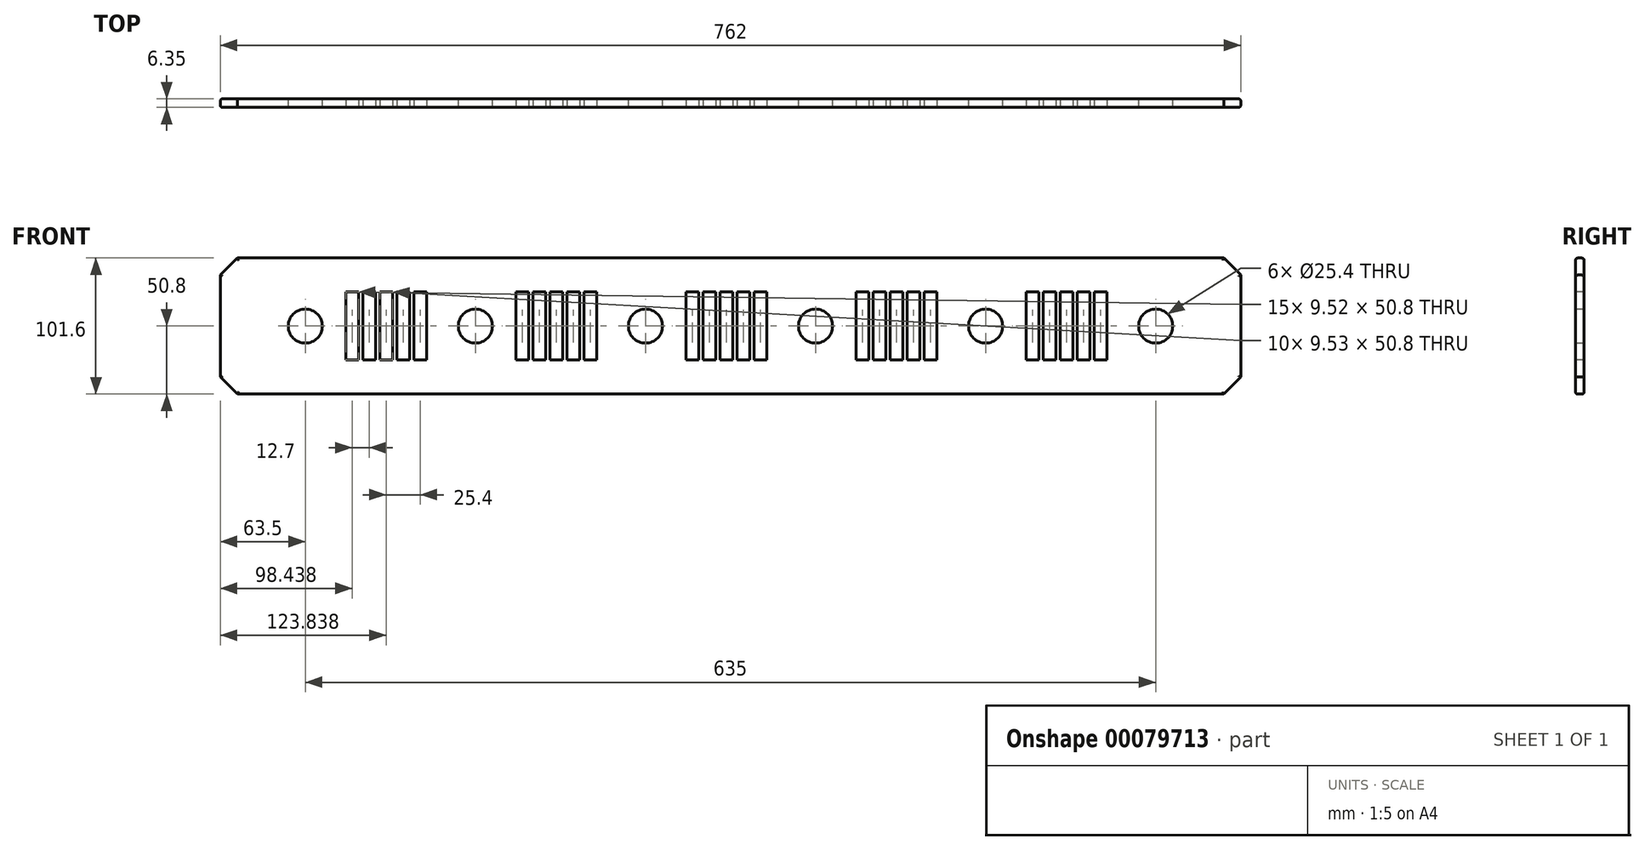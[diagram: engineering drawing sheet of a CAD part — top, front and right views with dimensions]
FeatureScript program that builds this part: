
annotation { "Feature Type Name" : "Feature", "Feature Type Description" : "" }
export const myFeature = defineFeature(function(context is Context, id is Id, definition is map)
    precondition{}
    {
        {
            var Q0;
            Q0=qCreatedBy(makeId("Front.planeOp"),FACE);
            var sketch = newSketch(context, id + "F0", { "sketchPlane" : qUnion([Q0])});
            skLineSegment(sketch, "E0.bottom", {"start": v(0, 0) * mm, "end": v(762, 0) * mm});
            skLineSegment(sketch, "E0.top", {"start": v(0, 101.6) * mm, "end": v(762, 101.6) * mm});
            skLineSegment(sketch, "E0.left", {"start": v(0, 0) * mm, "end": v(0, 101.6) * mm});
            skLineSegment(sketch, "E0.right", {"start": v(762, 0) * mm, "end": v(762, 101.6) * mm});
            skCircle(sketch, "E1", {"center": v(63.5, 50.8) * mm, "radius": 12.7 * mm});
            skPoint(sketch, "E1.centerSnap0", {"position": v(0, 50.8) * mm});
            skCircle(sketch, "E2", {"center": v(190.5, 50.8) * mm, "radius": 12.7 * mm});
            skCircle(sketch, "E3", {"center": v(317.5, 50.8) * mm, "radius": 12.7 * mm});
            skCircle(sketch, "E4", {"center": v(444.5, 50.8) * mm, "radius": 12.7 * mm});
            skCircle(sketch, "E5", {"center": v(571.5, 50.8) * mm, "radius": 12.7 * mm});
            skCircle(sketch, "E6", {"center": v(698.5, 50.8) * mm, "radius": 12.7 * mm});
            skSolve(sketch);
        }
        {
            var Q0;
            Q0 = qSketchRegion(id + "F0", true);
            extrude(context, id + "F1", {"entities" : qUnion([Q0]), "depth" : 6.35 * mm});
        }
        {
            var Q0;
            Q0=makeQuery(id+"F1.opExtrude","CAP_FACE",FACE,{"disambiguationData":[OSD([sQuery(id+"F0.wireOp",EDGE,"E0.bottom"),sQuery(id+"F0.wireOp",EDGE,"E0.top"),sQuery(id+"F0.wireOp",EDGE,"E0.left"),sQuery(id+"F0.wireOp",EDGE,"E0.right"),sQuery(id+"F0.wireOp",EDGE,"E1"),sQuery(id+"F0.wireOp",EDGE,"E2"),sQuery(id+"F0.wireOp",EDGE,"E3"),sQuery(id+"F0.wireOp",EDGE,"E4"),sQuery(id+"F0.wireOp",EDGE,"E5"),sQuery(id+"F0.wireOp",EDGE,"E6")])],"isStart":false});
            var sketch = newSketch(context, id + "F2", { "sketchPlane" : qUnion([Q0])});
            skLineSegment(sketch, "E7.bottom", {"start": v(93.68, 76.2) * mm, "end": v(103.2, 76.2) * mm});
            skLineSegment(sketch, "E7.top", {"start": v(93.68, 25.4) * mm, "end": v(103.2, 25.4) * mm});
            skLineSegment(sketch, "E7.left", {"start": v(93.68, 76.2) * mm, "end": v(93.68, 25.4) * mm});
            skLineSegment(sketch, "E7.right", {"start": v(103.2, 76.2) * mm, "end": v(103.2, 25.4) * mm});
            skLineSegment(sketch, "E8.1.0.0", {"start": v(106.38, 76.2) * mm, "end": v(115.9, 76.2) * mm});
            skLineSegment(sketch, "E8.1.0.1", {"start": v(106.38, 25.4) * mm, "end": v(115.9, 25.4) * mm});
            skLineSegment(sketch, "E8.1.0.2", {"start": v(106.38, 76.2) * mm, "end": v(106.38, 25.4) * mm});
            skLineSegment(sketch, "E8.1.0.3", {"start": v(115.9, 76.2) * mm, "end": v(115.9, 25.4) * mm});
            skLineSegment(sketch, "E8.2.0.0", {"start": v(119.08, 76.2) * mm, "end": v(128.6, 76.2) * mm});
            skLineSegment(sketch, "E8.2.0.1", {"start": v(119.08, 25.4) * mm, "end": v(128.6, 25.4) * mm});
            skLineSegment(sketch, "E8.2.0.2", {"start": v(119.08, 76.2) * mm, "end": v(119.08, 25.4) * mm});
            skLineSegment(sketch, "E8.2.0.3", {"start": v(128.6, 76.2) * mm, "end": v(128.6, 25.4) * mm});
            skLineSegment(sketch, "E8.3.0.0", {"start": v(131.78, 76.2) * mm, "end": v(141.3, 76.2) * mm});
            skLineSegment(sketch, "E8.3.0.1", {"start": v(131.78, 25.4) * mm, "end": v(141.3, 25.4) * mm});
            skLineSegment(sketch, "E8.3.0.2", {"start": v(131.78, 76.2) * mm, "end": v(131.78, 25.4) * mm});
            skLineSegment(sketch, "E8.3.0.3", {"start": v(141.3, 76.2) * mm, "end": v(141.3, 25.4) * mm});
            skLineSegment(sketch, "E8.4.0.0", {"start": v(144.48, 76.2) * mm, "end": v(154, 76.2) * mm});
            skLineSegment(sketch, "E8.4.0.1", {"start": v(144.48, 25.4) * mm, "end": v(154, 25.4) * mm});
            skLineSegment(sketch, "E8.4.0.2", {"start": v(144.48, 76.2) * mm, "end": v(144.48, 25.4) * mm});
            skLineSegment(sketch, "E8.4.0.3", {"start": v(154, 76.2) * mm, "end": v(154, 25.4) * mm});
            skLineSegment(sketch, "E8.direction1", {"start": v(93.68, 76.2) * mm, "end": v(106.38, 76.2) * mm, "construction": true});
            skLineSegment(sketch, "E9.bottom", {"start": v(220.68, 76.2) * mm, "end": v(230.2, 76.2) * mm});
            skLineSegment(sketch, "E9.top", {"start": v(220.68, 25.4) * mm, "end": v(230.2, 25.4) * mm});
            skLineSegment(sketch, "E9.left", {"start": v(220.68, 76.2) * mm, "end": v(220.68, 25.4) * mm});
            skLineSegment(sketch, "E9.right", {"start": v(230.2, 76.2) * mm, "end": v(230.2, 25.4) * mm});
            skLineSegment(sketch, "E10.1.0.0", {"start": v(233.38, 76.2) * mm, "end": v(233.38, 25.4) * mm});
            skLineSegment(sketch, "E10.1.0.1", {"start": v(242.9, 76.2) * mm, "end": v(242.9, 25.4) * mm});
            skLineSegment(sketch, "E10.1.0.2", {"start": v(233.38, 76.2) * mm, "end": v(242.9, 76.2) * mm});
            skLineSegment(sketch, "E10.1.0.3", {"start": v(233.38, 25.4) * mm, "end": v(242.9, 25.4) * mm});
            skLineSegment(sketch, "E10.2.0.0", {"start": v(246.08, 76.2) * mm, "end": v(246.08, 25.4) * mm});
            skLineSegment(sketch, "E10.2.0.1", {"start": v(255.6, 76.2) * mm, "end": v(255.6, 25.4) * mm});
            skLineSegment(sketch, "E10.2.0.2", {"start": v(246.08, 76.2) * mm, "end": v(255.6, 76.2) * mm});
            skLineSegment(sketch, "E10.2.0.3", {"start": v(246.08, 25.4) * mm, "end": v(255.6, 25.4) * mm});
            skLineSegment(sketch, "E10.3.0.0", {"start": v(258.78, 76.2) * mm, "end": v(258.78, 25.4) * mm});
            skLineSegment(sketch, "E10.3.0.1", {"start": v(268.3, 76.2) * mm, "end": v(268.3, 25.4) * mm});
            skLineSegment(sketch, "E10.3.0.2", {"start": v(258.78, 76.2) * mm, "end": v(268.3, 76.2) * mm});
            skLineSegment(sketch, "E10.3.0.3", {"start": v(258.78, 25.4) * mm, "end": v(268.3, 25.4) * mm});
            skLineSegment(sketch, "E10.4.0.0", {"start": v(271.48, 76.2) * mm, "end": v(271.48, 25.4) * mm});
            skLineSegment(sketch, "E10.4.0.1", {"start": v(281, 76.2) * mm, "end": v(281, 25.4) * mm});
            skLineSegment(sketch, "E10.4.0.2", {"start": v(271.48, 76.2) * mm, "end": v(281, 76.2) * mm});
            skLineSegment(sketch, "E10.4.0.3", {"start": v(271.48, 25.4) * mm, "end": v(281, 25.4) * mm});
            skLineSegment(sketch, "E10.direction1", {"start": v(220.68, 25.4) * mm, "end": v(233.38, 25.4) * mm, "construction": true});
            skLineSegment(sketch, "E11.bottom", {"start": v(347.68, 76.2) * mm, "end": v(357.2, 76.2) * mm});
            skLineSegment(sketch, "E11.top", {"start": v(347.68, 25.4) * mm, "end": v(357.2, 25.4) * mm});
            skLineSegment(sketch, "E11.left", {"start": v(347.68, 76.2) * mm, "end": v(347.68, 25.4) * mm});
            skLineSegment(sketch, "E11.right", {"start": v(357.2, 76.2) * mm, "end": v(357.2, 25.4) * mm});
            skLineSegment(sketch, "E12.1.0.0", {"start": v(360.38, 76.2) * mm, "end": v(369.9, 76.2) * mm});
            skLineSegment(sketch, "E12.1.0.1", {"start": v(360.38, 25.4) * mm, "end": v(369.9, 25.4) * mm});
            skLineSegment(sketch, "E12.1.0.2", {"start": v(360.38, 76.2) * mm, "end": v(360.38, 25.4) * mm});
            skLineSegment(sketch, "E12.1.0.3", {"start": v(369.9, 76.2) * mm, "end": v(369.9, 25.4) * mm});
            skLineSegment(sketch, "E12.2.0.0", {"start": v(373.08, 76.2) * mm, "end": v(382.6, 76.2) * mm});
            skLineSegment(sketch, "E12.2.0.1", {"start": v(373.08, 25.4) * mm, "end": v(382.6, 25.4) * mm});
            skLineSegment(sketch, "E12.2.0.2", {"start": v(373.08, 76.2) * mm, "end": v(373.08, 25.4) * mm});
            skLineSegment(sketch, "E12.2.0.3", {"start": v(382.6, 76.2) * mm, "end": v(382.6, 25.4) * mm});
            skLineSegment(sketch, "E12.3.0.0", {"start": v(385.78, 76.2) * mm, "end": v(395.3, 76.2) * mm});
            skLineSegment(sketch, "E12.3.0.1", {"start": v(385.78, 25.4) * mm, "end": v(395.3, 25.4) * mm});
            skLineSegment(sketch, "E12.3.0.2", {"start": v(385.78, 76.2) * mm, "end": v(385.78, 25.4) * mm});
            skLineSegment(sketch, "E12.3.0.3", {"start": v(395.3, 76.2) * mm, "end": v(395.3, 25.4) * mm});
            skLineSegment(sketch, "E12.4.0.0", {"start": v(398.48, 76.2) * mm, "end": v(408, 76.2) * mm});
            skLineSegment(sketch, "E12.4.0.1", {"start": v(398.48, 25.4) * mm, "end": v(408, 25.4) * mm});
            skLineSegment(sketch, "E12.4.0.2", {"start": v(398.48, 76.2) * mm, "end": v(398.48, 25.4) * mm});
            skLineSegment(sketch, "E12.4.0.3", {"start": v(408, 76.2) * mm, "end": v(408, 25.4) * mm});
            skLineSegment(sketch, "E12.direction1", {"start": v(347.68, 76.2) * mm, "end": v(360.38, 76.2) * mm, "construction": true});
            skLineSegment(sketch, "E13.bottom", {"start": v(474.68, 76.2) * mm, "end": v(484.2, 76.2) * mm});
            skLineSegment(sketch, "E13.top", {"start": v(474.68, 25.4) * mm, "end": v(484.2, 25.4) * mm});
            skLineSegment(sketch, "E13.left", {"start": v(474.68, 76.2) * mm, "end": v(474.68, 25.4) * mm});
            skLineSegment(sketch, "E13.right", {"start": v(484.2, 76.2) * mm, "end": v(484.2, 25.4) * mm});
            skLineSegment(sketch, "E14.1.0.0", {"start": v(487.38, 76.2) * mm, "end": v(487.38, 25.4) * mm});
            skLineSegment(sketch, "E14.1.0.1", {"start": v(496.9, 76.2) * mm, "end": v(496.9, 25.4) * mm});
            skLineSegment(sketch, "E14.1.0.2", {"start": v(487.38, 76.2) * mm, "end": v(496.9, 76.2) * mm});
            skLineSegment(sketch, "E14.1.0.3", {"start": v(487.38, 25.4) * mm, "end": v(496.9, 25.4) * mm});
            skLineSegment(sketch, "E14.2.0.0", {"start": v(500.08, 76.2) * mm, "end": v(500.08, 25.4) * mm});
            skLineSegment(sketch, "E14.2.0.1", {"start": v(509.6, 76.2) * mm, "end": v(509.6, 25.4) * mm});
            skLineSegment(sketch, "E14.2.0.2", {"start": v(500.08, 76.2) * mm, "end": v(509.6, 76.2) * mm});
            skLineSegment(sketch, "E14.2.0.3", {"start": v(500.08, 25.4) * mm, "end": v(509.6, 25.4) * mm});
            skLineSegment(sketch, "E14.3.0.0", {"start": v(512.78, 76.2) * mm, "end": v(512.78, 25.4) * mm});
            skLineSegment(sketch, "E14.3.0.1", {"start": v(522.3, 76.2) * mm, "end": v(522.3, 25.4) * mm});
            skLineSegment(sketch, "E14.3.0.2", {"start": v(512.78, 76.2) * mm, "end": v(522.3, 76.2) * mm});
            skLineSegment(sketch, "E14.3.0.3", {"start": v(512.78, 25.4) * mm, "end": v(522.3, 25.4) * mm});
            skLineSegment(sketch, "E14.4.0.0", {"start": v(525.48, 76.2) * mm, "end": v(525.48, 25.4) * mm});
            skLineSegment(sketch, "E14.4.0.1", {"start": v(535, 76.2) * mm, "end": v(535, 25.4) * mm});
            skLineSegment(sketch, "E14.4.0.2", {"start": v(525.48, 76.2) * mm, "end": v(535, 76.2) * mm});
            skLineSegment(sketch, "E14.4.0.3", {"start": v(525.48, 25.4) * mm, "end": v(535, 25.4) * mm});
            skLineSegment(sketch, "E14.direction1", {"start": v(474.68, 25.4) * mm, "end": v(487.38, 25.4) * mm, "construction": true});
            skLineSegment(sketch, "E15.bottom", {"start": v(601.68, 76.2) * mm, "end": v(611.2, 76.2) * mm});
            skLineSegment(sketch, "E15.top", {"start": v(601.68, 25.4) * mm, "end": v(611.2, 25.4) * mm});
            skLineSegment(sketch, "E15.left", {"start": v(601.68, 76.2) * mm, "end": v(601.68, 25.4) * mm});
            skLineSegment(sketch, "E15.right", {"start": v(611.2, 76.2) * mm, "end": v(611.2, 25.4) * mm});
            skLineSegment(sketch, "E16.1.0.0", {"start": v(614.38, 76.2) * mm, "end": v(623.9, 76.2) * mm});
            skLineSegment(sketch, "E16.1.0.1", {"start": v(614.38, 76.2) * mm, "end": v(614.38, 25.4) * mm});
            skLineSegment(sketch, "E16.1.0.2", {"start": v(623.9, 76.2) * mm, "end": v(623.9, 25.4) * mm});
            skLineSegment(sketch, "E16.1.0.3", {"start": v(614.38, 25.4) * mm, "end": v(623.9, 25.4) * mm});
            skLineSegment(sketch, "E16.2.0.0", {"start": v(627.08, 76.2) * mm, "end": v(636.6, 76.2) * mm});
            skLineSegment(sketch, "E16.2.0.1", {"start": v(627.08, 76.2) * mm, "end": v(627.08, 25.4) * mm});
            skLineSegment(sketch, "E16.2.0.2", {"start": v(636.6, 76.2) * mm, "end": v(636.6, 25.4) * mm});
            skLineSegment(sketch, "E16.2.0.3", {"start": v(627.08, 25.4) * mm, "end": v(636.6, 25.4) * mm});
            skLineSegment(sketch, "E16.3.0.0", {"start": v(639.78, 76.2) * mm, "end": v(649.3, 76.2) * mm});
            skLineSegment(sketch, "E16.3.0.1", {"start": v(639.78, 76.2) * mm, "end": v(639.78, 25.4) * mm});
            skLineSegment(sketch, "E16.3.0.2", {"start": v(649.3, 76.2) * mm, "end": v(649.3, 25.4) * mm});
            skLineSegment(sketch, "E16.3.0.3", {"start": v(639.78, 25.4) * mm, "end": v(649.3, 25.4) * mm});
            skLineSegment(sketch, "E16.4.0.0", {"start": v(652.48, 76.2) * mm, "end": v(662, 76.2) * mm});
            skLineSegment(sketch, "E16.4.0.1", {"start": v(652.48, 76.2) * mm, "end": v(652.48, 25.4) * mm});
            skLineSegment(sketch, "E16.4.0.2", {"start": v(662, 76.2) * mm, "end": v(662, 25.4) * mm});
            skLineSegment(sketch, "E16.4.0.3", {"start": v(652.48, 25.4) * mm, "end": v(662, 25.4) * mm});
            skLineSegment(sketch, "E16.direction1", {"start": v(601.68, 76.2) * mm, "end": v(614.38, 76.2) * mm, "construction": true});
            skSolve(sketch);
        }
        {
            var Q0;
            Q0 = qSketchRegion(id + "F2", true);
            extrude(context, id + "F3", {"entities" : qUnion([Q0]), "operationType" : NewBodyOperationType.REMOVE, "endBound" : BoundingType.THROUGH_ALL, "oppositeDirection" : true, "depth" : 25.4 * mm});
        }
        {
            var Q0;
            Q0=makeQuery(id+"F1.opExtrude","SWEPT_EDGE",EDGE,{"disambiguationData":[OSD([sQuery(id+"F0.wireOp",EDGE,"E0.top"),sQuery(id+"F0.wireOp",EDGE,"E0.left")])]});
            var Q1;
            Q1=makeQuery(id+"F1.opExtrude","SWEPT_EDGE",EDGE,{"disambiguationData":[OSD([sQuery(id+"F0.wireOp",EDGE,"E0.bottom"),sQuery(id+"F0.wireOp",EDGE,"E0.left")])]});
            var Q2;
            Q2=makeQuery(id+"F1.opExtrude","SWEPT_EDGE",EDGE,{"disambiguationData":[OSD([sQuery(id+"F0.wireOp",EDGE,"E0.top"),sQuery(id+"F0.wireOp",EDGE,"E0.right")])]});
            var Q3;
            Q3=makeQuery(id+"F1.opExtrude","SWEPT_EDGE",EDGE,{"disambiguationData":[OSD([sQuery(id+"F0.wireOp",EDGE,"E0.bottom"),sQuery(id+"F0.wireOp",EDGE,"E0.right")])]});
            chamfer(context, id + "F4", {"entities" : qUnion([Q0, Q1, Q2, Q3]), "width" : 12.7 * mm, "tangentPropagation" : true});
        }
        {
            var Q0;
            Q0=makeQuery(id+"F1.opExtrude","CAP_EDGE",EDGE,{"disambiguationData":[OSD([sQuery(id+"F0.wireOp",EDGE,"E0.top")])],"isStart":false});
            var Q1;
            Q1=makeQuery(id+"F1.opExtrude","CAP_EDGE",EDGE,{"disambiguationData":[OSD([sQuery(id+"F0.wireOp",EDGE,"E0.top")])],"isStart":true});
            var Q2;
            Q2=makeQuery(id+"F1.opExtrude","CAP_EDGE",EDGE,{"disambiguationData":[OSD([sQuery(id+"F0.wireOp",EDGE,"E0.bottom")])],"isStart":false});
            var Q3;
            Q3=makeQuery(id+"F1.opExtrude","CAP_EDGE",EDGE,{"disambiguationData":[OSD([sQuery(id+"F0.wireOp",EDGE,"E0.bottom")])],"isStart":true});
            var Q4;
            {var subQ0=sQuery(id+"F0.wireOp",EDGE,"E0.left");var subQ1=sQuery(id+"F0.wireOp",EDGE,"E0.top");Q4=makeQuery(id+"F4.opChamfer","BLEND_EDGE",EDGE,{"blendedFrom":[makeQuery(id+"F1.opExtrude","SWEPT_EDGE",EDGE,{"disambiguationData":[OSD([subQ1,subQ0])]}),makeQuery(id+"F1.opExtrude","CAP_FACE",FACE,{"disambiguationData":[OSD([sQuery(id+"F0.wireOp",EDGE,"E0.bottom"),subQ1,subQ0,sQuery(id+"F0.wireOp",EDGE,"E0.right"),sQuery(id+"F0.wireOp",EDGE,"E1"),sQuery(id+"F0.wireOp",EDGE,"E2"),sQuery(id+"F0.wireOp",EDGE,"E3"),sQuery(id+"F0.wireOp",EDGE,"E4"),sQuery(id+"F0.wireOp",EDGE,"E5"),sQuery(id+"F0.wireOp",EDGE,"E6")])],"isStart":false})],"blendedInto":[makeQuery(id+"F1.opExtrude","CAP_FACE",FACE,{"disambiguationData":[OSD([sQuery(id+"F0.wireOp",EDGE,"E0.bottom"),subQ1,subQ0,sQuery(id+"F0.wireOp",EDGE,"E0.right"),sQuery(id+"F0.wireOp",EDGE,"E1"),sQuery(id+"F0.wireOp",EDGE,"E2"),sQuery(id+"F0.wireOp",EDGE,"E3"),sQuery(id+"F0.wireOp",EDGE,"E4"),sQuery(id+"F0.wireOp",EDGE,"E5"),sQuery(id+"F0.wireOp",EDGE,"E6")])],"isStart":false})]});}
            var Q5;
            {var subQ0=sQuery(id+"F0.wireOp",EDGE,"E0.left");var subQ1=sQuery(id+"F0.wireOp",EDGE,"E0.top");Q5=makeQuery(id+"F4.opChamfer","BLEND_EDGE",EDGE,{"blendedFrom":[makeQuery(id+"F1.opExtrude","SWEPT_EDGE",EDGE,{"disambiguationData":[OSD([subQ1,subQ0])]}),makeQuery(id+"F1.opExtrude","CAP_FACE",FACE,{"disambiguationData":[OSD([sQuery(id+"F0.wireOp",EDGE,"E0.bottom"),subQ1,subQ0,sQuery(id+"F0.wireOp",EDGE,"E0.right"),sQuery(id+"F0.wireOp",EDGE,"E1"),sQuery(id+"F0.wireOp",EDGE,"E2"),sQuery(id+"F0.wireOp",EDGE,"E3"),sQuery(id+"F0.wireOp",EDGE,"E4"),sQuery(id+"F0.wireOp",EDGE,"E5"),sQuery(id+"F0.wireOp",EDGE,"E6")])],"isStart":true})],"blendedInto":[makeQuery(id+"F1.opExtrude","CAP_FACE",FACE,{"disambiguationData":[OSD([sQuery(id+"F0.wireOp",EDGE,"E0.bottom"),subQ1,subQ0,sQuery(id+"F0.wireOp",EDGE,"E0.right"),sQuery(id+"F0.wireOp",EDGE,"E1"),sQuery(id+"F0.wireOp",EDGE,"E2"),sQuery(id+"F0.wireOp",EDGE,"E3"),sQuery(id+"F0.wireOp",EDGE,"E4"),sQuery(id+"F0.wireOp",EDGE,"E5"),sQuery(id+"F0.wireOp",EDGE,"E6")])],"isStart":true})]});}
            var Q6;
            Q6=makeQuery(id+"F1.opExtrude","CAP_EDGE",EDGE,{"disambiguationData":[OSD([sQuery(id+"F0.wireOp",EDGE,"E0.left")])],"isStart":false});
            var Q7;
            Q7=makeQuery(id+"F1.opExtrude","CAP_EDGE",EDGE,{"disambiguationData":[OSD([sQuery(id+"F0.wireOp",EDGE,"E0.left")])],"isStart":true});
            var Q8;
            {var subQ0=sQuery(id+"F0.wireOp",EDGE,"E0.left");var subQ1=sQuery(id+"F0.wireOp",EDGE,"E0.bottom");Q8=makeQuery(id+"F4.opChamfer","BLEND_EDGE",EDGE,{"blendedFrom":[makeQuery(id+"F1.opExtrude","SWEPT_EDGE",EDGE,{"disambiguationData":[OSD([subQ1,subQ0])]}),makeQuery(id+"F1.opExtrude","CAP_FACE",FACE,{"disambiguationData":[OSD([subQ1,sQuery(id+"F0.wireOp",EDGE,"E0.top"),subQ0,sQuery(id+"F0.wireOp",EDGE,"E0.right"),sQuery(id+"F0.wireOp",EDGE,"E1"),sQuery(id+"F0.wireOp",EDGE,"E2"),sQuery(id+"F0.wireOp",EDGE,"E3"),sQuery(id+"F0.wireOp",EDGE,"E4"),sQuery(id+"F0.wireOp",EDGE,"E5"),sQuery(id+"F0.wireOp",EDGE,"E6")])],"isStart":false})],"blendedInto":[makeQuery(id+"F1.opExtrude","CAP_FACE",FACE,{"disambiguationData":[OSD([subQ1,sQuery(id+"F0.wireOp",EDGE,"E0.top"),subQ0,sQuery(id+"F0.wireOp",EDGE,"E0.right"),sQuery(id+"F0.wireOp",EDGE,"E1"),sQuery(id+"F0.wireOp",EDGE,"E2"),sQuery(id+"F0.wireOp",EDGE,"E3"),sQuery(id+"F0.wireOp",EDGE,"E4"),sQuery(id+"F0.wireOp",EDGE,"E5"),sQuery(id+"F0.wireOp",EDGE,"E6")])],"isStart":false})]});}
            var Q9;
            {var subQ0=sQuery(id+"F0.wireOp",EDGE,"E0.left");var subQ1=sQuery(id+"F0.wireOp",EDGE,"E0.bottom");Q9=makeQuery(id+"F4.opChamfer","BLEND_EDGE",EDGE,{"blendedFrom":[makeQuery(id+"F1.opExtrude","SWEPT_EDGE",EDGE,{"disambiguationData":[OSD([subQ1,subQ0])]}),makeQuery(id+"F1.opExtrude","CAP_FACE",FACE,{"disambiguationData":[OSD([subQ1,sQuery(id+"F0.wireOp",EDGE,"E0.top"),subQ0,sQuery(id+"F0.wireOp",EDGE,"E0.right"),sQuery(id+"F0.wireOp",EDGE,"E1"),sQuery(id+"F0.wireOp",EDGE,"E2"),sQuery(id+"F0.wireOp",EDGE,"E3"),sQuery(id+"F0.wireOp",EDGE,"E4"),sQuery(id+"F0.wireOp",EDGE,"E5"),sQuery(id+"F0.wireOp",EDGE,"E6")])],"isStart":true})],"blendedInto":[makeQuery(id+"F1.opExtrude","CAP_FACE",FACE,{"disambiguationData":[OSD([subQ1,sQuery(id+"F0.wireOp",EDGE,"E0.top"),subQ0,sQuery(id+"F0.wireOp",EDGE,"E0.right"),sQuery(id+"F0.wireOp",EDGE,"E1"),sQuery(id+"F0.wireOp",EDGE,"E2"),sQuery(id+"F0.wireOp",EDGE,"E3"),sQuery(id+"F0.wireOp",EDGE,"E4"),sQuery(id+"F0.wireOp",EDGE,"E5"),sQuery(id+"F0.wireOp",EDGE,"E6")])],"isStart":true})]});}
            var Q10;
            {var subQ0=sQuery(id+"F0.wireOp",EDGE,"E0.right");var subQ1=sQuery(id+"F0.wireOp",EDGE,"E0.top");Q10=makeQuery(id+"F4.opChamfer","BLEND_EDGE",EDGE,{"blendedFrom":[makeQuery(id+"F1.opExtrude","SWEPT_EDGE",EDGE,{"disambiguationData":[OSD([subQ1,subQ0])]}),makeQuery(id+"F1.opExtrude","CAP_FACE",FACE,{"disambiguationData":[OSD([sQuery(id+"F0.wireOp",EDGE,"E0.bottom"),subQ1,sQuery(id+"F0.wireOp",EDGE,"E0.left"),subQ0,sQuery(id+"F0.wireOp",EDGE,"E1"),sQuery(id+"F0.wireOp",EDGE,"E2"),sQuery(id+"F0.wireOp",EDGE,"E3"),sQuery(id+"F0.wireOp",EDGE,"E4"),sQuery(id+"F0.wireOp",EDGE,"E5"),sQuery(id+"F0.wireOp",EDGE,"E6")])],"isStart":false})],"blendedInto":[makeQuery(id+"F1.opExtrude","CAP_FACE",FACE,{"disambiguationData":[OSD([sQuery(id+"F0.wireOp",EDGE,"E0.bottom"),subQ1,sQuery(id+"F0.wireOp",EDGE,"E0.left"),subQ0,sQuery(id+"F0.wireOp",EDGE,"E1"),sQuery(id+"F0.wireOp",EDGE,"E2"),sQuery(id+"F0.wireOp",EDGE,"E3"),sQuery(id+"F0.wireOp",EDGE,"E4"),sQuery(id+"F0.wireOp",EDGE,"E5"),sQuery(id+"F0.wireOp",EDGE,"E6")])],"isStart":false})]});}
            var Q11;
            {var subQ0=sQuery(id+"F0.wireOp",EDGE,"E0.right");var subQ1=sQuery(id+"F0.wireOp",EDGE,"E0.top");Q11=makeQuery(id+"F4.opChamfer","BLEND_EDGE",EDGE,{"blendedFrom":[makeQuery(id+"F1.opExtrude","SWEPT_EDGE",EDGE,{"disambiguationData":[OSD([subQ1,subQ0])]}),makeQuery(id+"F1.opExtrude","CAP_FACE",FACE,{"disambiguationData":[OSD([sQuery(id+"F0.wireOp",EDGE,"E0.bottom"),subQ1,sQuery(id+"F0.wireOp",EDGE,"E0.left"),subQ0,sQuery(id+"F0.wireOp",EDGE,"E1"),sQuery(id+"F0.wireOp",EDGE,"E2"),sQuery(id+"F0.wireOp",EDGE,"E3"),sQuery(id+"F0.wireOp",EDGE,"E4"),sQuery(id+"F0.wireOp",EDGE,"E5"),sQuery(id+"F0.wireOp",EDGE,"E6")])],"isStart":true})],"blendedInto":[makeQuery(id+"F1.opExtrude","CAP_FACE",FACE,{"disambiguationData":[OSD([sQuery(id+"F0.wireOp",EDGE,"E0.bottom"),subQ1,sQuery(id+"F0.wireOp",EDGE,"E0.left"),subQ0,sQuery(id+"F0.wireOp",EDGE,"E1"),sQuery(id+"F0.wireOp",EDGE,"E2"),sQuery(id+"F0.wireOp",EDGE,"E3"),sQuery(id+"F0.wireOp",EDGE,"E4"),sQuery(id+"F0.wireOp",EDGE,"E5"),sQuery(id+"F0.wireOp",EDGE,"E6")])],"isStart":true})]});}
            var Q12;
            Q12=makeQuery(id+"F1.opExtrude","CAP_EDGE",EDGE,{"disambiguationData":[OSD([sQuery(id+"F0.wireOp",EDGE,"E0.right")])],"isStart":false});
            var Q13;
            Q13=makeQuery(id+"F1.opExtrude","CAP_EDGE",EDGE,{"disambiguationData":[OSD([sQuery(id+"F0.wireOp",EDGE,"E0.right")])],"isStart":true});
            var Q14;
            {var subQ0=sQuery(id+"F0.wireOp",EDGE,"E0.right");var subQ1=sQuery(id+"F0.wireOp",EDGE,"E0.bottom");Q14=makeQuery(id+"F4.opChamfer","BLEND_EDGE",EDGE,{"blendedFrom":[makeQuery(id+"F1.opExtrude","SWEPT_EDGE",EDGE,{"disambiguationData":[OSD([subQ1,subQ0])]}),makeQuery(id+"F1.opExtrude","CAP_FACE",FACE,{"disambiguationData":[OSD([subQ1,sQuery(id+"F0.wireOp",EDGE,"E0.top"),sQuery(id+"F0.wireOp",EDGE,"E0.left"),subQ0,sQuery(id+"F0.wireOp",EDGE,"E1"),sQuery(id+"F0.wireOp",EDGE,"E2"),sQuery(id+"F0.wireOp",EDGE,"E3"),sQuery(id+"F0.wireOp",EDGE,"E4"),sQuery(id+"F0.wireOp",EDGE,"E5"),sQuery(id+"F0.wireOp",EDGE,"E6")])],"isStart":false})],"blendedInto":[makeQuery(id+"F1.opExtrude","CAP_FACE",FACE,{"disambiguationData":[OSD([subQ1,sQuery(id+"F0.wireOp",EDGE,"E0.top"),sQuery(id+"F0.wireOp",EDGE,"E0.left"),subQ0,sQuery(id+"F0.wireOp",EDGE,"E1"),sQuery(id+"F0.wireOp",EDGE,"E2"),sQuery(id+"F0.wireOp",EDGE,"E3"),sQuery(id+"F0.wireOp",EDGE,"E4"),sQuery(id+"F0.wireOp",EDGE,"E5"),sQuery(id+"F0.wireOp",EDGE,"E6")])],"isStart":false})]});}
            var Q15;
            {var subQ0=sQuery(id+"F0.wireOp",EDGE,"E0.right");var subQ1=sQuery(id+"F0.wireOp",EDGE,"E0.bottom");Q15=makeQuery(id+"F4.opChamfer","BLEND_EDGE",EDGE,{"blendedFrom":[makeQuery(id+"F1.opExtrude","SWEPT_EDGE",EDGE,{"disambiguationData":[OSD([subQ1,subQ0])]}),makeQuery(id+"F1.opExtrude","CAP_FACE",FACE,{"disambiguationData":[OSD([subQ1,sQuery(id+"F0.wireOp",EDGE,"E0.top"),sQuery(id+"F0.wireOp",EDGE,"E0.left"),subQ0,sQuery(id+"F0.wireOp",EDGE,"E1"),sQuery(id+"F0.wireOp",EDGE,"E2"),sQuery(id+"F0.wireOp",EDGE,"E3"),sQuery(id+"F0.wireOp",EDGE,"E4"),sQuery(id+"F0.wireOp",EDGE,"E5"),sQuery(id+"F0.wireOp",EDGE,"E6")])],"isStart":true})],"blendedInto":[makeQuery(id+"F1.opExtrude","CAP_FACE",FACE,{"disambiguationData":[OSD([subQ1,sQuery(id+"F0.wireOp",EDGE,"E0.top"),sQuery(id+"F0.wireOp",EDGE,"E0.left"),subQ0,sQuery(id+"F0.wireOp",EDGE,"E1"),sQuery(id+"F0.wireOp",EDGE,"E2"),sQuery(id+"F0.wireOp",EDGE,"E3"),sQuery(id+"F0.wireOp",EDGE,"E4"),sQuery(id+"F0.wireOp",EDGE,"E5"),sQuery(id+"F0.wireOp",EDGE,"E6")])],"isStart":true})]});}
            fillet(context, id + "F5", {"entities" : qUnion([Q0, Q1, Q2, Q3, Q4, Q5, Q6, Q7, Q8, Q9, Q10, Q11, Q12, Q13, Q14, Q15]), "radius" : 1.6 * mm, "tangentPropagation" : true, "allowEdgeOverflow" : false});
        }
    });
